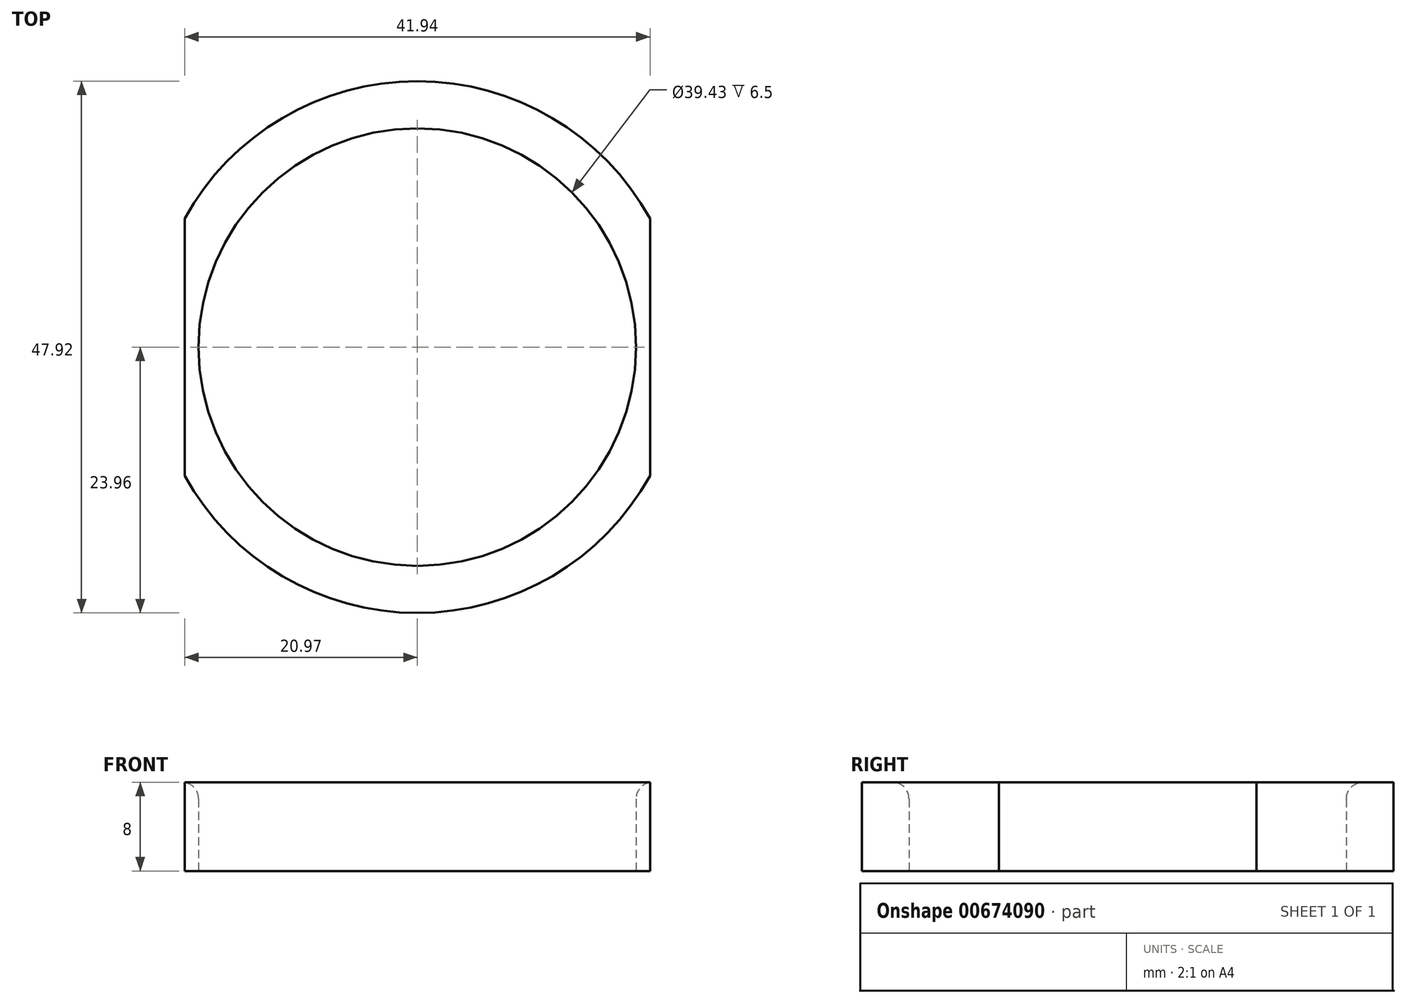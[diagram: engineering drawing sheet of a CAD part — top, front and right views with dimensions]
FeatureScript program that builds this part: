
annotation { "Feature Type Name" : "Feature", "Feature Type Description" : "" }
export const myFeature = defineFeature(function(context is Context, id is Id, definition is map)
    precondition{}
    {
        {
            var Q0;
            Q0=qCreatedBy(makeId("Top.planeOp"),FACE);
            var sketch = newSketch(context, id + "F0", { "sketchPlane" : qUnion([Q0])});
            skCircle(sketch, "E0", {"center": v(0, 0) * mm, "radius": 23.96 * mm});
            skLineSegment(sketch, "E1.bottom", {"start": v(20.97, 30.02) * mm, "end": v(-20.97, 30.02) * mm});
            skLineSegment(sketch, "E1.top", {"start": v(20.97, -30.02) * mm, "end": v(-20.97, -30.02) * mm});
            skLineSegment(sketch, "E1.left", {"start": v(20.97, 30.02) * mm, "end": v(20.97, -30.02) * mm});
            skLineSegment(sketch, "E1.right", {"start": v(-20.97, 30.02) * mm, "end": v(-20.97, -30.02) * mm});
            skCircle(sketch, "E2", {"center": v(0, 0) * mm, "radius": 14.16 * mm});
            skCircle(sketch, "E3", {"center": v(0, 0) * mm, "radius": 18.38 * mm});
            skCircle(sketch, "E4", {"center": v(0, 0) * mm, "radius": 19.71 * mm});
            skSolve(sketch);
        }
        {
            var Q0;
            Q0=makeQuery(id+"F0.imprint","IMPRINT",FACE,{"disambiguationData":[TD([[makeQuery(id+"F0.imprint","IMPRINT",EDGE,{"derivedFrom":sQuery(id+"F0.wireOp",EDGE,"E4")}),-1.0]])]});
            extrude(context, id + "F1", {"entities" : qUnion([Q0]), "depth" : 8 * mm, "offsetDistance" : 25 * mm});
        }
        {
            var Q0;
            Q0=makeQuery(id+"F1.opExtrude","CAP_EDGE",EDGE,{"disambiguationData":[OSD([sQuery(id+"F0.wireOp",EDGE,"E4")])],"isStart":false});
            fillet(context, id + "F2", {"entities" : qUnion([Q0]), "radius" : 1.5 * mm, "tangentPropagation" : true, "allowEdgeOverflow" : false});
        }
    });
